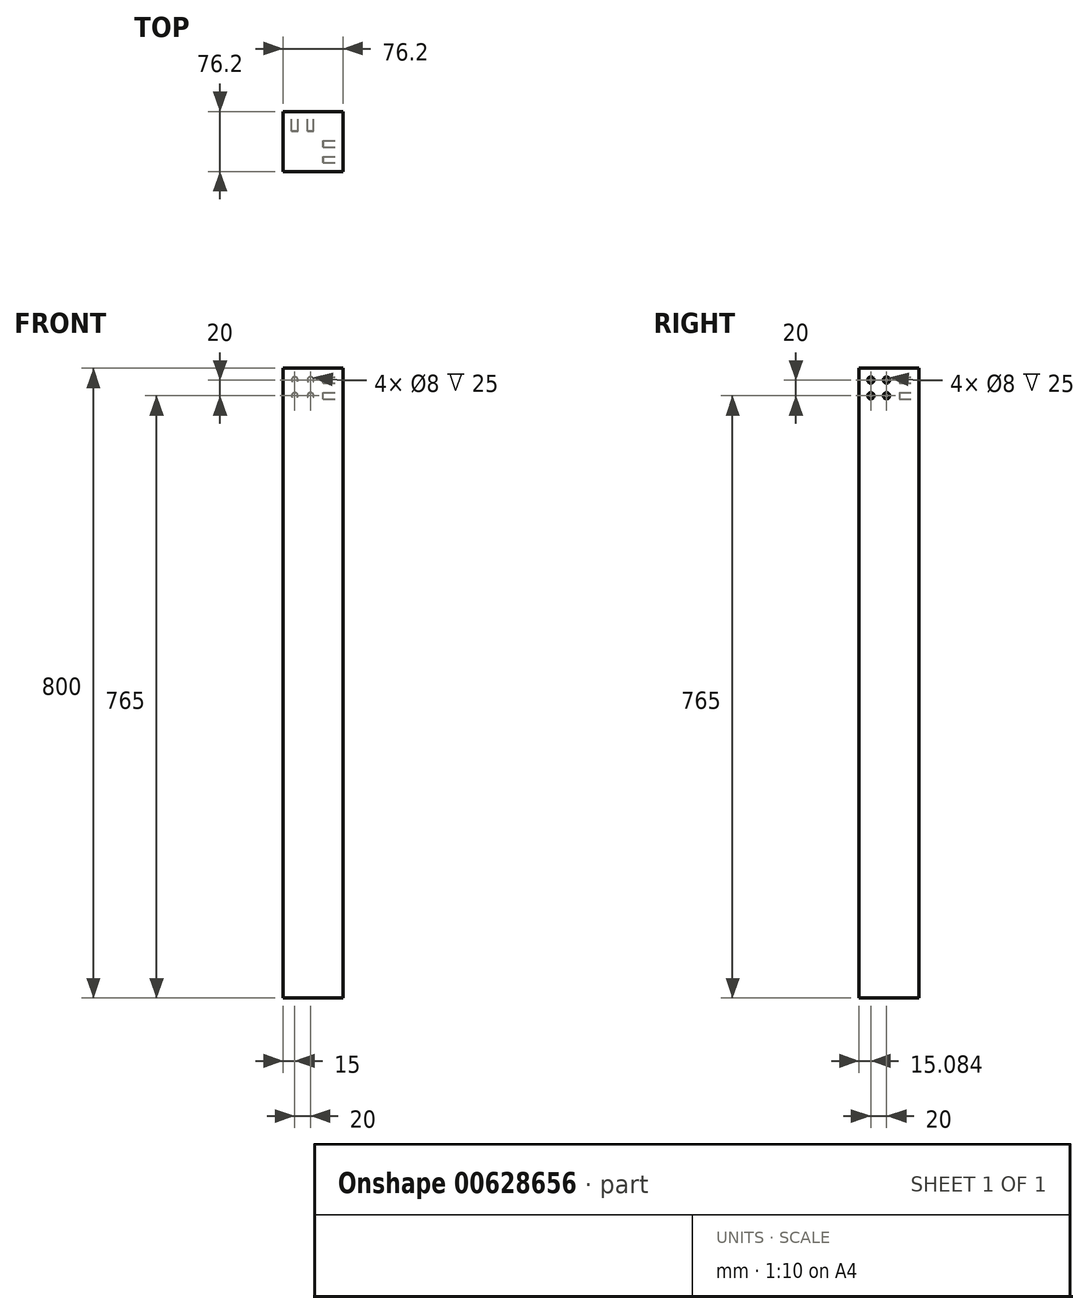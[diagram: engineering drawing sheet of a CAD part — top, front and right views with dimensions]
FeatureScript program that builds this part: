
annotation { "Feature Type Name" : "Feature", "Feature Type Description" : "" }
export const myFeature = defineFeature(function(context is Context, id is Id, definition is map)
    precondition{}
    {
        {
            var Q0;
            Q0=qCreatedBy(makeId("Top.planeOp"),FACE);
            var sketch = newSketch(context, id + "F0", { "sketchPlane" : qUnion([Q0])});
            skLineSegment(sketch, "E0.bottom", {"start": v(-38.1, 38.1) * mm, "end": v(38.1, 38.1) * mm});
            skLineSegment(sketch, "E0.top", {"start": v(-38.1, -38.1) * mm, "end": v(38.1, -38.1) * mm});
            skLineSegment(sketch, "E0.left", {"start": v(-38.1, 38.1) * mm, "end": v(-38.1, -38.1) * mm});
            skLineSegment(sketch, "E0.right", {"start": v(38.1, 38.1) * mm, "end": v(38.1, -38.1) * mm});
            skPoint(sketch, "E0.middle", {"position": v(0, 0) * mm});
            skSolve(sketch);
        }
        {
            var Q0;
            Q0 = qSketchRegion(id + "F0", true);
            extrude(context, id + "F1", {"entities" : qUnion([Q0]), "oppositeDirection" : true, "depth" : 800 * mm, "offsetDistance" : 25 * mm});
        }
        {
            var Q0;
            Q0=makeQuery(id+"F1.opExtrude","SWEPT_FACE",FACE,{"disambiguationData":[OSD([sQuery(id+"F0.wireOp",EDGE,"E0.right")])]});
            var sketch = newSketch(context, id + "F2", { "sketchPlane" : qUnion([Q0])});
            skLineSegment(sketch, "E1.bottom", {"start": v(-38.02, 0) * mm, "end": v(11.98, 0) * mm});
            skLineSegment(sketch, "E1.top", {"start": v(-38.02, -50) * mm, "end": v(11.98, -50) * mm});
            skLineSegment(sketch, "E1.left", {"start": v(-38.02, 0) * mm, "end": v(-38.02, -50) * mm});
            skLineSegment(sketch, "E1.right", {"start": v(11.98, 0) * mm, "end": v(11.98, -50) * mm});
            skCircle(sketch, "E2", {"center": v(-23.02, -15) * mm, "radius": 4 * mm});
            skCircle(sketch, "E3", {"center": v(-3.02, -15) * mm, "radius": 4 * mm});
            skCircle(sketch, "E4", {"center": v(-23.02, -35) * mm, "radius": 4 * mm});
            skCircle(sketch, "E5", {"center": v(-3.02, -35) * mm, "radius": 4 * mm});
            skSolve(sketch);
        }
        {
            var Q0;
            Q0=makeQuery(id+"F2.imprint","IMPRINT",FACE,{"disambiguationData":[TD([[makeQuery(id+"F2.imprint","IMPRINT",EDGE,{"derivedFrom":sQuery(id+"F2.wireOp",EDGE,"E2")}),1.0]])]});
            var Q1;
            Q1=makeQuery(id+"F2.imprint","IMPRINT",FACE,{"disambiguationData":[TD([[makeQuery(id+"F2.imprint","IMPRINT",EDGE,{"derivedFrom":sQuery(id+"F2.wireOp",EDGE,"E3")}),1.0]])]});
            var Q2;
            Q2=makeQuery(id+"F2.imprint","IMPRINT",FACE,{"disambiguationData":[TD([[makeQuery(id+"F2.imprint","IMPRINT",EDGE,{"derivedFrom":sQuery(id+"F2.wireOp",EDGE,"E5")}),1.0]])]});
            var Q3;
            Q3=makeQuery(id+"F2.imprint","IMPRINT",FACE,{"disambiguationData":[TD([[makeQuery(id+"F2.imprint","IMPRINT",EDGE,{"derivedFrom":sQuery(id+"F2.wireOp",EDGE,"E4")}),1.0]])]});
            extrude(context, id + "F3", {"entities" : qUnion([Q0, Q1, Q2, Q3]), "operationType" : NewBodyOperationType.REMOVE, "oppositeDirection" : true, "depth" : 25 * mm, "offsetDistance" : 25 * mm});
        }
        {
            var Q0;
            Q0=makeQuery(id+"F1.opExtrude","SWEPT_FACE",FACE,{"disambiguationData":[OSD([sQuery(id+"F0.wireOp",EDGE,"E0.bottom")])]});
            var sketch = newSketch(context, id + "F4", { "sketchPlane" : qUnion([Q0])});
            skLineSegment(sketch, "E6.bottom", {"start": v(38.1, 0) * mm, "end": v(-11.9, 0) * mm});
            skLineSegment(sketch, "E6.top", {"start": v(38.1, -50) * mm, "end": v(-11.9, -50) * mm});
            skLineSegment(sketch, "E6.left", {"start": v(38.1, 0) * mm, "end": v(38.1, -50) * mm});
            skLineSegment(sketch, "E6.right", {"start": v(-11.9, 0) * mm, "end": v(-11.9, -50) * mm});
            skCircle(sketch, "E7", {"center": v(3.1, -15) * mm, "radius": 4 * mm});
            skCircle(sketch, "E8", {"center": v(23.1, -15) * mm, "radius": 4 * mm});
            skCircle(sketch, "E9", {"center": v(23.1, -35) * mm, "radius": 4 * mm});
            skCircle(sketch, "E10", {"center": v(3.1, -35) * mm, "radius": 4 * mm});
            skSolve(sketch);
        }
        {
            var Q0;
            Q0=makeQuery(id+"F4.imprint","IMPRINT",FACE,{"disambiguationData":[TD([[makeQuery(id+"F4.imprint","IMPRINT",EDGE,{"derivedFrom":sQuery(id+"F4.wireOp",EDGE,"E7")}),1.0]])]});
            var Q1;
            Q1=makeQuery(id+"F4.imprint","IMPRINT",FACE,{"disambiguationData":[TD([[makeQuery(id+"F4.imprint","IMPRINT",EDGE,{"derivedFrom":sQuery(id+"F4.wireOp",EDGE,"E8")}),1.0]])]});
            var Q2;
            Q2=makeQuery(id+"F4.imprint","IMPRINT",FACE,{"disambiguationData":[TD([[makeQuery(id+"F4.imprint","IMPRINT",EDGE,{"derivedFrom":sQuery(id+"F4.wireOp",EDGE,"E10")}),1.0]])]});
            var Q3;
            Q3=makeQuery(id+"F4.imprint","IMPRINT",FACE,{"disambiguationData":[TD([[makeQuery(id+"F4.imprint","IMPRINT",EDGE,{"derivedFrom":sQuery(id+"F4.wireOp",EDGE,"E9")}),1.0]])]});
            extrude(context, id + "F5", {"entities" : qUnion([Q0, Q1, Q2, Q3]), "operationType" : NewBodyOperationType.REMOVE, "oppositeDirection" : true, "depth" : 25 * mm, "offsetDistance" : 25 * mm});
        }
    });
